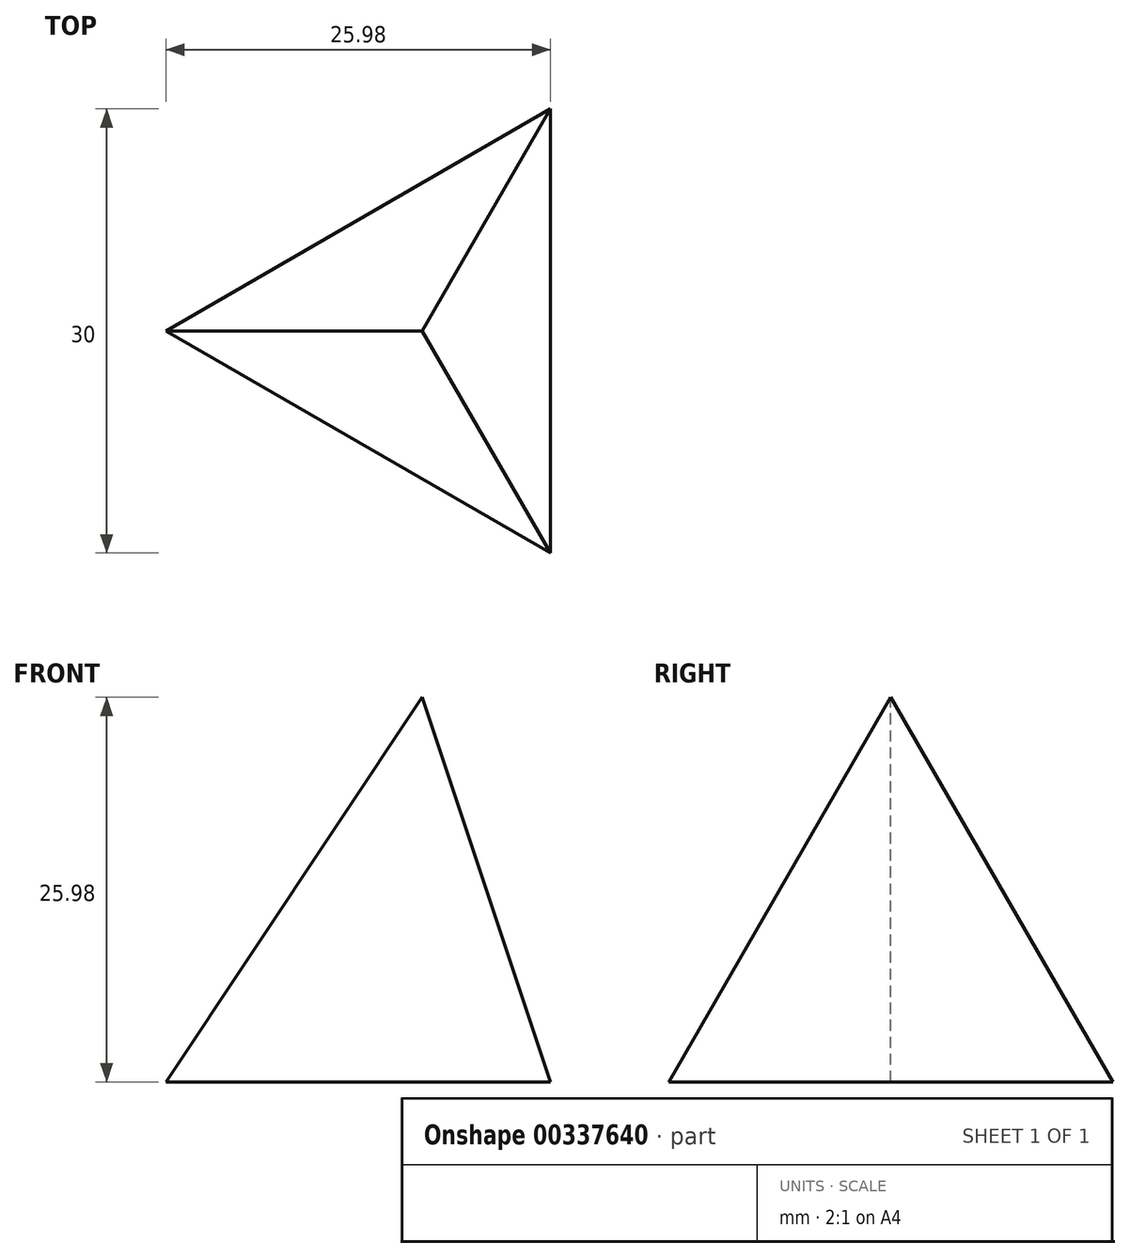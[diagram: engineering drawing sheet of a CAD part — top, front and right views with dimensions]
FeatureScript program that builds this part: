
annotation { "Feature Type Name" : "Feature", "Feature Type Description" : "" }
export const myFeature = defineFeature(function(context is Context, id is Id, definition is map)
    precondition{}
    {
        {
            var Q0;
            Q0=qCreatedBy(makeId("Top.planeOp"),FACE);
            var sketch = newSketch(context, id + "F0", { "sketchPlane" : qUnion([Q0])});
            skCircle(sketch, "E0.cCircle", {"center": v(0, 0) * mm, "radius": 8.66 * mm, "construction": true});
            skLineSegment(sketch, "E0.0", {"start": v(8.66, 15) * mm, "end": v(8.66, -15) * mm});
            skLineSegment(sketch, "E0.1", {"start": v(8.66, -15) * mm, "end": v(-17.32, 0) * mm});
            skLineSegment(sketch, "E0.2", {"start": v(-17.32, 0) * mm, "end": v(8.66, 15) * mm});
            skPoint(sketch, "E0.0.midPoint", {"position": v(8.66, 0) * mm});
            skSolve(sketch);
        }
        {
            var Q0;
            Q0=qCreatedBy(makeId("Front.planeOp"),FACE);
            var sketch = newSketch(context, id + "F1", { "sketchPlane" : qUnion([Q0])});
            skLineSegment(sketch, "E1", {"start": v(8.66, 0) * mm, "end": v(0, 0) * mm, "construction": true});
            skLineSegment(sketch, "E2", {"start": v(-17.32, 0) * mm, "end": v(8.66, 0) * mm, "construction": true});
            skLineSegment(sketch, "E3", {"start": v(0, 0) * mm, "end": v(0, 25.98) * mm});
            skSolve(sketch);
        }
        {
            var Q0;
            Q0=makeQuery(id+"F0.imprint","IMPRINT",FACE,{"disambiguationData":[TD([[makeQuery(id+"F0.imprint","IMPRINT",EDGE,{"derivedFrom":sQuery(id+"F0.wireOp",EDGE,"E0.0")}),-1.0]])]});
            var Q1;
            Q1=sQuery(id+"F1.wireOp",VERTEX,"E3.end");
            loft(context, id + "F2", {"sheetProfilesArray" : [{ "sheetProfileEntities" : qUnion([Q0]) }, { "sheetProfileEntities" : qUnion([Q1]) }]});
        }
    });
